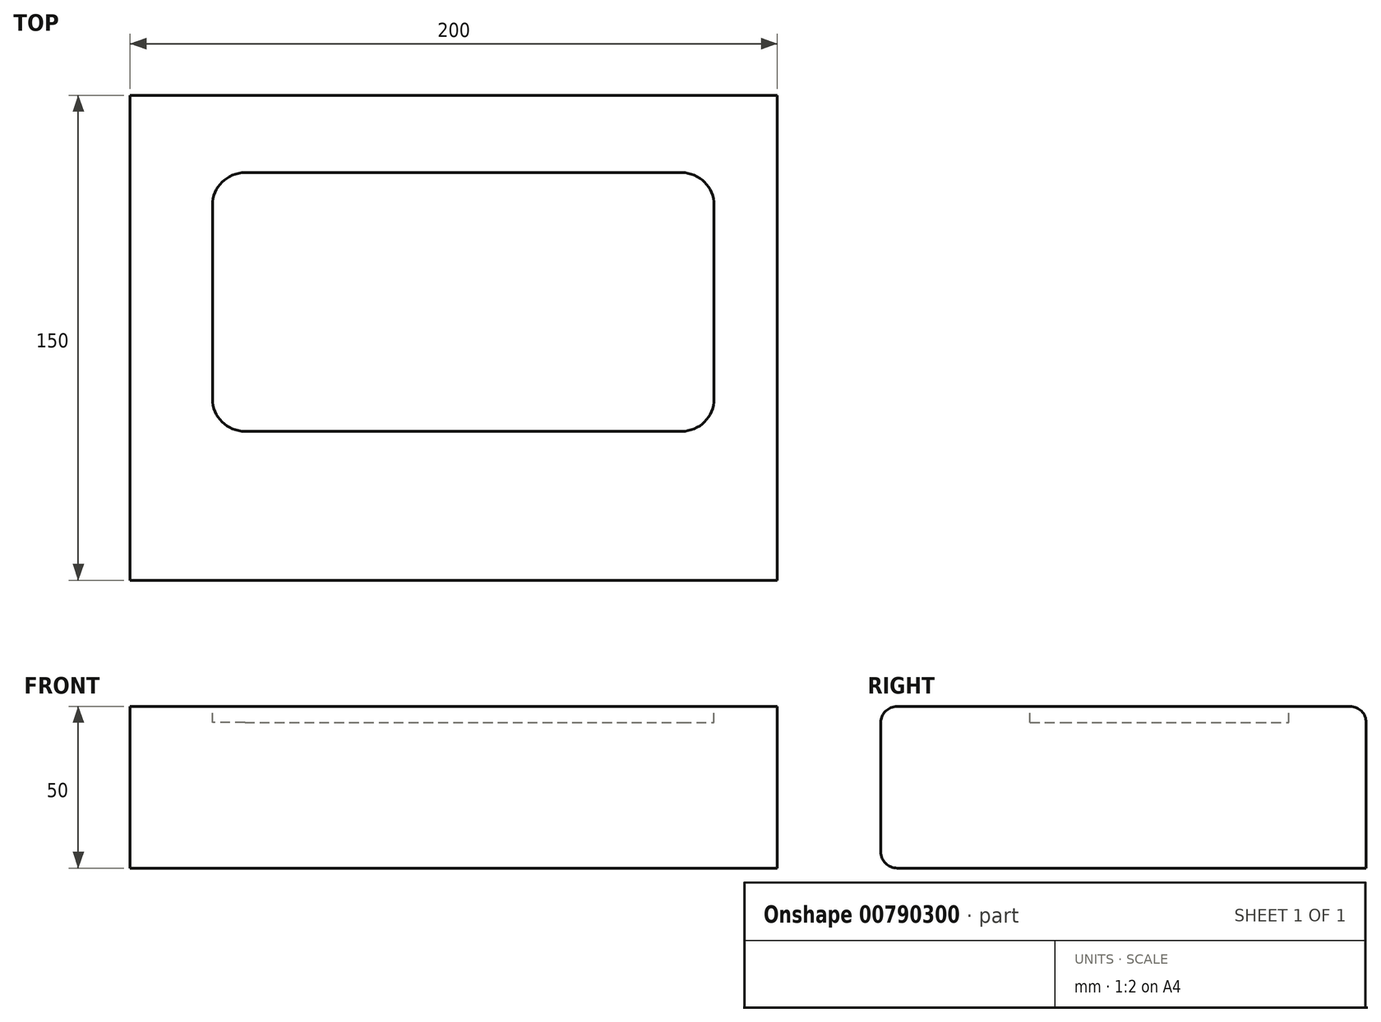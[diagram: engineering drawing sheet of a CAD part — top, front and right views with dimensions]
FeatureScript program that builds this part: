
annotation { "Feature Type Name" : "Feature", "Feature Type Description" : "" }
export const myFeature = defineFeature(function(context is Context, id is Id, definition is map)
    precondition{}
    {
        {
            var Q0;
            Q0=qCreatedBy(makeId("Right.planeOp"),FACE);
            var sketch = newSketch(context, id + "F0", { "sketchPlane" : qUnion([Q0])});
            skLineSegment(sketch, "E0.top", {"start": v(-18.8, -18.04) * mm, "end": v(126.2, -18.04) * mm});
            skLineSegment(sketch, "E0.right", {"start": v(126.2, 26.96) * mm, "end": v(126.2, -18.04) * mm});
            skPoint(sketch, "E1.visualSharp", {"position": v(11.2, 31.96) * mm});
            skPoint(sketch, "E2.visualSharp", {"position": v(-23.8, -3.04) * mm});
            skPoint(sketch, "E3.visualSharp", {"position": v(-23.8, -18.04) * mm});
            skArc(sketch, "E3.filletArc", {"start": v(-23.8, -13.04) * mm, "mid": v(-22.34, -16.57) * mm, "end": v(-18.8, -18.04) * mm});
            skPoint(sketch, "E4.visualSharp", {"position": v(126.2, 31.96) * mm});
            skArc(sketch, "E4.filletArc", {"start": v(126.2, 26.96) * mm, "mid": v(124.73, 30.5) * mm, "end": v(121.2, 31.96) * mm});
            skLineSegment(sketch, "E5", {"start": v(-23.8, 26.96) * mm, "end": v(-23.8, -13.04) * mm});
            skLineSegment(sketch, "E6", {"start": v(121.2, 31.96) * mm, "end": v(-18.8, 31.96) * mm});
            skPoint(sketch, "E7.orphan", {"position": v(-23.8, 47.6) * mm});
            skPoint(sketch, "E8.visualSharp", {"position": v(-23.8, 31.96) * mm});
            skArc(sketch, "E8.filletArc", {"start": v(-18.8, 31.96) * mm, "mid": v(-22.34, 30.5) * mm, "end": v(-23.8, 26.96) * mm});
            skSolve(sketch);
        }
        {
            var Q0;
            Q0=makeQuery(id+"F0.imprint","IMPRINT",FACE,{"disambiguationData":[TD([[makeQuery(id+"F0.imprint","IMPRINT",EDGE,{"derivedFrom":sQuery(id+"F0.wireOp",EDGE,"E0.top")}),1.0]])]});
            extrude(context, id + "F1", {"entities" : qUnion([Q0]), "depth" : 200 * mm, "offsetDistance" : 25 * mm});
        }
        {
            var Q0;
            Q0=makeQuery(id+"F1.opExtrude","SWEPT_FACE",FACE,{"disambiguationData":[OSD([sQuery(id+"F0.wireOp",EDGE,"E6")])]});
            var sketch = newSketch(context, id + "F2", { "sketchPlane" : qUnion([Q0])});
            skLineSegment(sketch, "E9.bottom", {"start": v(35.45, 22.28) * mm, "end": v(170.45, 22.28) * mm});
            skLineSegment(sketch, "E9.top", {"start": v(35.45, 102.28) * mm, "end": v(170.45, 102.28) * mm});
            skLineSegment(sketch, "E9.left", {"start": v(25.45, 32.28) * mm, "end": v(25.45, 92.28) * mm});
            skLineSegment(sketch, "E9.right", {"start": v(180.45, 32.28) * mm, "end": v(180.45, 92.28) * mm});
            skPoint(sketch, "E10.visualSharp", {"position": v(180.45, 22.28) * mm});
            skArc(sketch, "E10.filletArc", {"start": v(170.45, 22.28) * mm, "mid": v(177.53, 25.2) * mm, "end": v(180.45, 32.28) * mm});
            skPoint(sketch, "E11.visualSharp", {"position": v(180.45, 102.28) * mm});
            skArc(sketch, "E11.filletArc", {"start": v(180.45, 92.28) * mm, "mid": v(177.53, 99.35) * mm, "end": v(170.45, 102.28) * mm});
            skPoint(sketch, "E12.visualSharp", {"position": v(25.45, 22.28) * mm});
            skArc(sketch, "E12.filletArc", {"start": v(25.45, 32.28) * mm, "mid": v(28.38, 25.2) * mm, "end": v(35.45, 22.28) * mm});
            skPoint(sketch, "E13.visualSharp", {"position": v(25.45, 102.28) * mm});
            skArc(sketch, "E13.filletArc", {"start": v(35.45, 102.28) * mm, "mid": v(28.38, 99.35) * mm, "end": v(25.45, 92.28) * mm});
            skSolve(sketch);
        }
        {
            var Q0;
            Q0=qSketchRegion(id+"F2",true);
            extrude(context, id + "F3", {"entities" : qUnion([Q0]), "operationType" : NewBodyOperationType.REMOVE, "oppositeDirection" : true, "depth" : 5 * mm, "offsetDistance" : 25 * mm});
        }
    });
